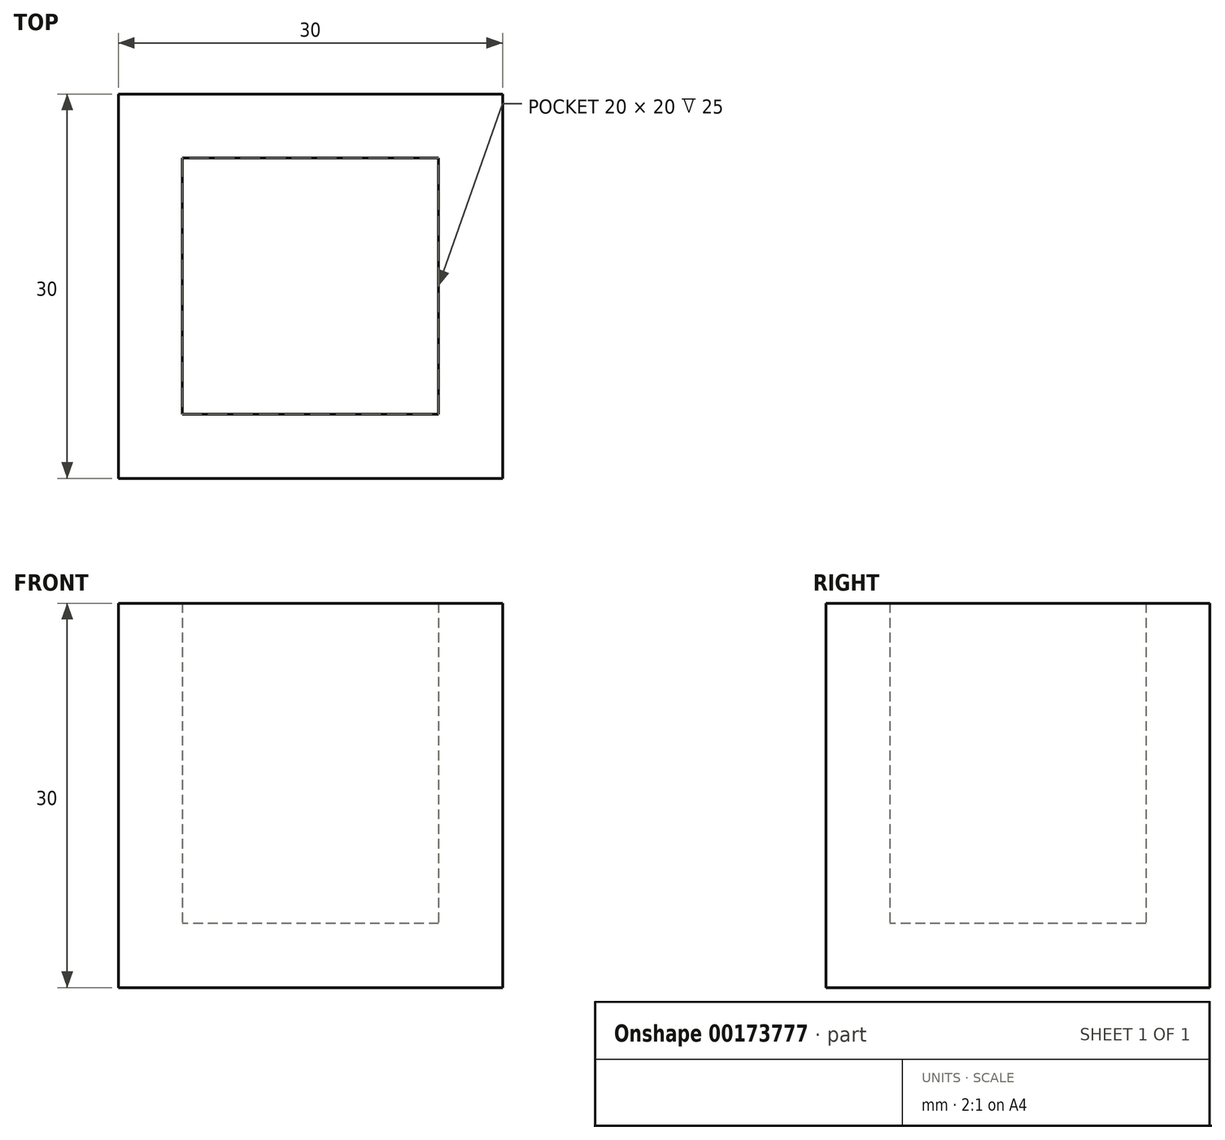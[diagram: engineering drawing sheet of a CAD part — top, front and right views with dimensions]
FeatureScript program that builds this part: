
annotation { "Feature Type Name" : "Feature", "Feature Type Description" : "" }
export const myFeature = defineFeature(function(context is Context, id is Id, definition is map)
    precondition{}
    {
        {
            var Q0;
            Q0=qCreatedBy(makeId("Top.planeOp"),FACE);
            var sketch = newSketch(context, id + "F0", { "sketchPlane" : qUnion([Q0])});
            skPoint(sketch, "E0.middle", {"position": v(0, 0) * mm});
            skLineSegment(sketch, "E1.bottom", {"start": v(15, 15) * mm, "end": v(-15, 15) * mm});
            skLineSegment(sketch, "E1.top", {"start": v(15, -15) * mm, "end": v(-15, -15) * mm});
            skLineSegment(sketch, "E1.left", {"start": v(15, 15) * mm, "end": v(15, -15) * mm});
            skLineSegment(sketch, "E1.right", {"start": v(-15, 15) * mm, "end": v(-15, -15) * mm});
            skSolve(sketch);
        }
        {
            var Q0;
            Q0 = qSketchRegion(id + "F0", true);
            extrude(context, id + "F1", {"entities" : qUnion([Q0]), "depth" : 30 * mm});
        }
        {
            var Q0;
            Q0=makeQuery(id+"F1.opExtrude","CAP_FACE",FACE,{"disambiguationData":[OSD([sQuery(id+"F0.wireOp",EDGE,"E1.bottom"),sQuery(id+"F0.wireOp",EDGE,"E1.top"),sQuery(id+"F0.wireOp",EDGE,"E1.left"),sQuery(id+"F0.wireOp",EDGE,"E1.right")])],"isStart":false});
            shell(context, id + "F2", {"entities" : qUnion([Q0]), "thickness" : 5 * mm});
        }
    });
